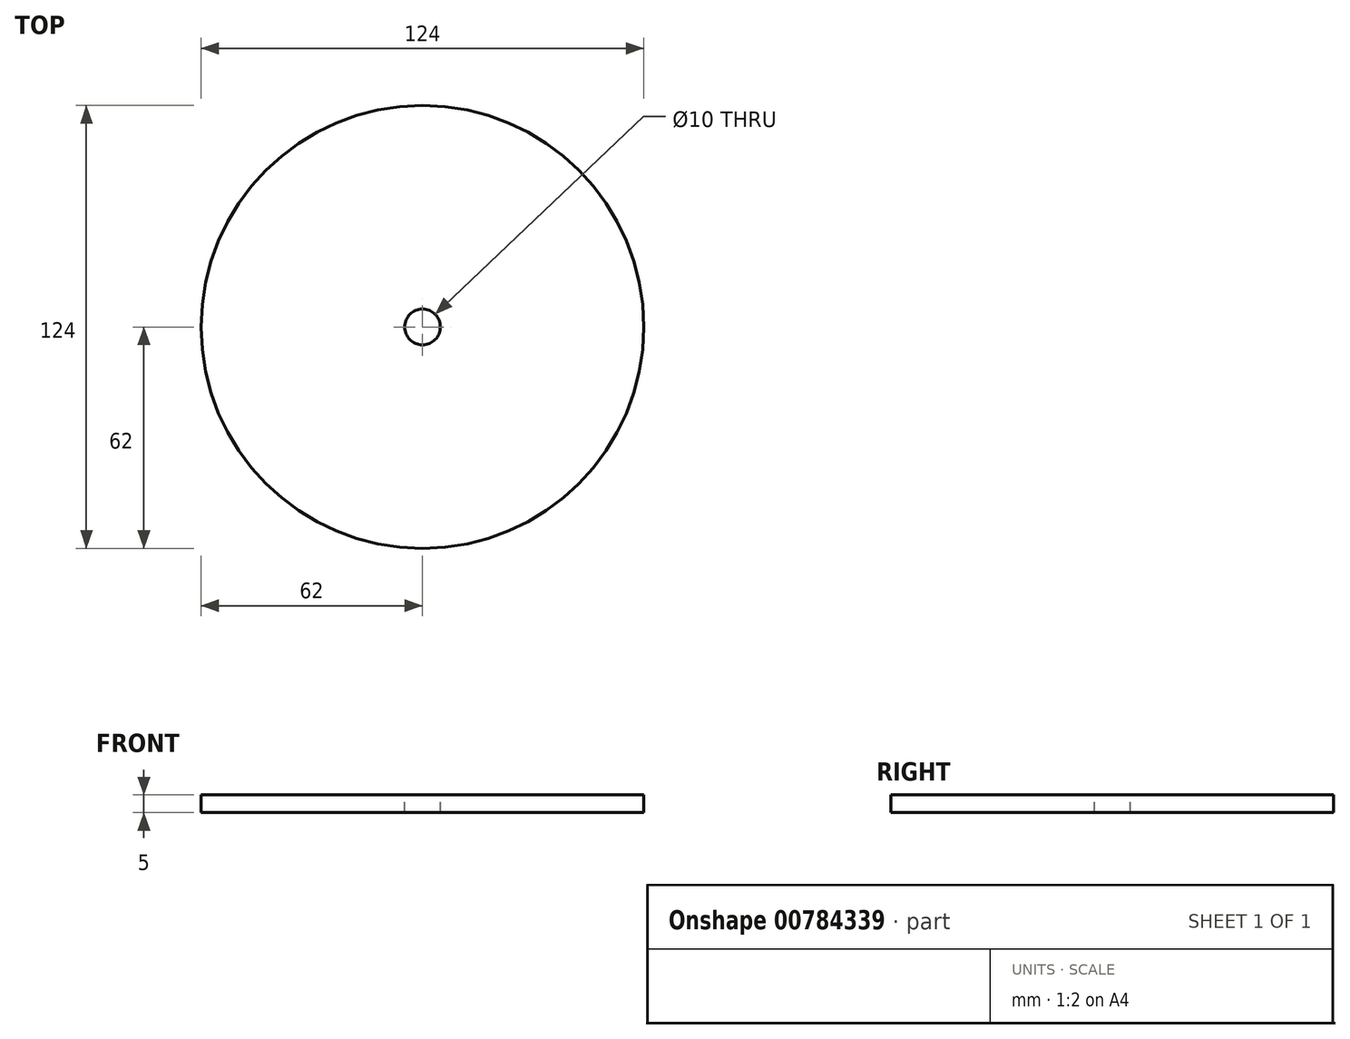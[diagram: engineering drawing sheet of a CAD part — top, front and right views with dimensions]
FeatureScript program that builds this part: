
annotation { "Feature Type Name" : "Feature", "Feature Type Description" : "" }
export const myFeature = defineFeature(function(context is Context, id is Id, definition is map)
    precondition{}
    {
        {
            var Q0;
            Q0=qCreatedBy(makeId("Top.planeOp"),FACE);
            var sketch = newSketch(context, id + "F0", { "sketchPlane" : qUnion([Q0])});
            skCircle(sketch, "E0", {"center": v(0, 0) * mm, "radius": 62 * mm});
            skSolve(sketch);
        }
        {
            var Q0;
            Q0=qCreatedBy(makeId("Top.planeOp"),FACE);
            var sketch = newSketch(context, id + "F1", { "sketchPlane" : qUnion([Q0])});
            skCircle(sketch, "E1", {"center": v(0, 0) * mm, "radius": 5 * mm});
            skSolve(sketch);
        }
        {
            var Q0;
            Q0=sQuery(id+"F1.wireOp",EDGE,"E1");
            extrude(context, id + "F2", {"bodyType" : ToolBodyType.SURFACE, "surfaceEntities" : qUnion([Q0]), "depth" : 10 * mm, "offsetDistance" : 25 * mm});
        }
        {
            var Q0;
            Q0 = qSketchRegion(id + "F0", true);
            extrude(context, id + "F3", {"entities" : qUnion([Q0]), "oppositeDirection" : true, "depth" : 5 * mm, "offsetDistance" : 25 * mm});
        }
        {
            var Q0;
            Q0 = qSketchRegion(id + "F1", true);
            extrude(context, id + "F4", {"entities" : qUnion([Q0]), "operationType" : NewBodyOperationType.REMOVE, "oppositeDirection" : true, "depth" : 25 * mm, "offsetDistance" : 25 * mm});
        }
    });
